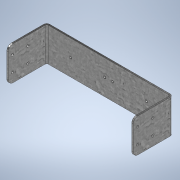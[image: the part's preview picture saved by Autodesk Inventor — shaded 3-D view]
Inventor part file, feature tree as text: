
AUTODESK INVENTOR PART (.ipt)
format: ipt  version: 2022 (Build 260153000, 153)  size: 218,112 bytes
history: native  units: mm
features: sheet_metal_op x4, sketch x4, other x3, hole x2, chamfer x1
ambient origin geometry x8: Origin, YZ Plane, XZ Plane, XY Plane, X Axis, Y Axis, Z Axis, Center Point
bodies: Solid1 (feature_tree)
feature tree (14):
  sheet_metal_op  "Face1"
  sheet_metal_op  "Flange1"
  hole  "Hole1"  [1 undecoded]
  chamfer  "Corner Round1"
  hole  "Hole2"  [1 undecoded]
  sketch  "Sketch1"  dims[d0=161.0mm d1=44.0mm]
  other  "Plate1"
  sketch  "Sketch2"  dims[d2=2.0mm d3=2.0mm]
  other  "Plate2"
  sheet_metal_op  "Bend1"
  sheet_metal_op  "Corner1"
  sketch  "Sketch3"  dims[d4=1.0mm]
  sketch  "Sketch4"  dims[d5=4.0mm d6=2.0mm d7=52.0mm d8=90.0deg d9=2.0mm d10=8.0mm d11=2.0mm d12=2.0mm d13=20.0mm d14=20.0mm d15=5.5mm d16=3.4mm d17=6.0mm d18=6.3mm d19=2.0mm d20=90.0deg d21=2.0mm d22=20.594885mm d23=6.0mm d24=10.0mm d25=33.0mm d26=33.0mm d27=44.5mm d28=44.5mm d29=3.4mm d30=6.0mm d31=4.0mm d32=2.0mm d33=90.0deg d34=8.0mm d35=20.594885mm]
  other  "Definition1"
note: 2 required parameter values undecoded (feature->parameter linkage not recoverable at this tier; creation-order binding heuristic only, values carry confidence <= 0.55)
